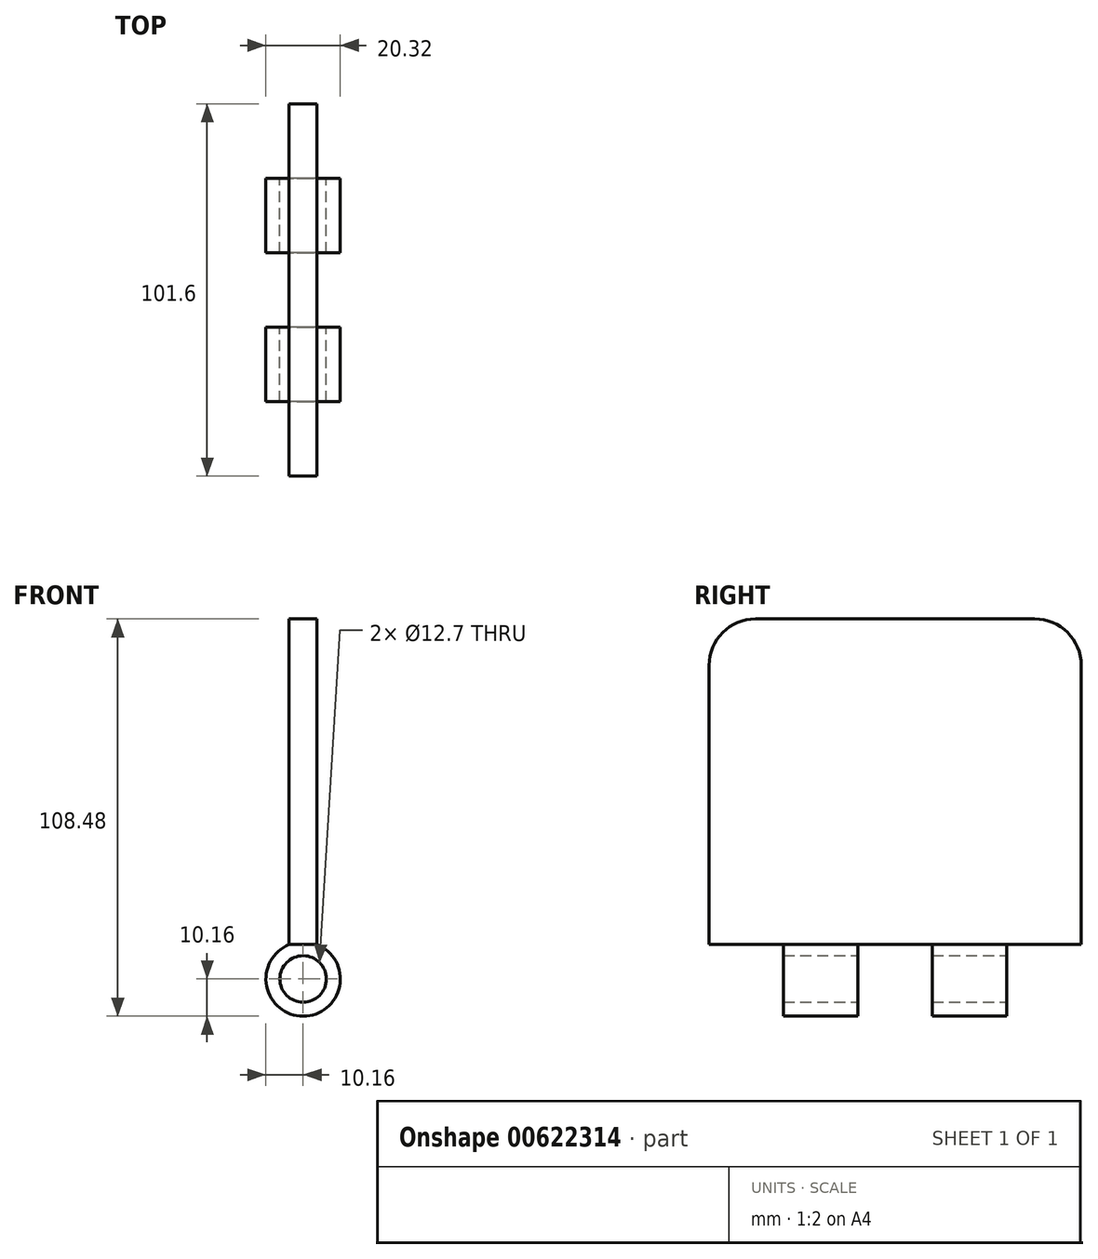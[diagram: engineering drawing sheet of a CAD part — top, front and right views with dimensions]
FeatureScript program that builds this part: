
annotation { "Feature Type Name" : "Feature", "Feature Type Description" : "" }
export const myFeature = defineFeature(function(context is Context, id is Id, definition is map)
    precondition{}
    {
        {
            var Q0;
            Q0=qCreatedBy(makeId("Front.planeOp"),FACE);
            var sketch = newSketch(context, id + "F0", { "sketchPlane" : qUnion([Q0])});
            skLineSegment(sketch, "E0", {"start": v(-3.81, 9.42) * mm, "end": v(-3.81, 98.32) * mm});
            skLineSegment(sketch, "E1", {"start": v(-3.81, 98.32) * mm, "end": v(3.8, 98.32) * mm});
            skLineSegment(sketch, "E2", {"start": v(3.8, 98.32) * mm, "end": v(3.81, 9.42) * mm});
            skArc(sketch, "E3", {"start": v(-3.81, 9.42) * mm, "mid": v(0, -10.16) * mm, "end": v(3.81, 9.42) * mm});
            skSolve(sketch);
        }
        {
            var Q0;
            Q0=makeQuery(id+"F0.imprint","IMPRINT",FACE,{"disambiguationData":[TD([[makeQuery(id+"F0.imprint","IMPRINT",EDGE,{"derivedFrom":sQuery(id+"F0.wireOp",EDGE,"E0")}),-1.0]])]});
            extrude(context, id + "F1", {"entities" : qUnion([Q0]), "depth" : 101.6 * mm, "offsetDistance" : 25.4 * mm, "symmetric" : true});
        }
        {
            var Q0;
            Q0=makeQuery(id+"F1.opExtrude","CAP_EDGE",EDGE,{"disambiguationData":[OSD([sQuery(id+"F0.wireOp",EDGE,"E1")])],"isStart":false});
            var Q1;
            Q1=makeQuery(id+"F1.opExtrude","CAP_EDGE",EDGE,{"disambiguationData":[OSD([sQuery(id+"F0.wireOp",EDGE,"E1")])],"isStart":true});
            fillet(context, id + "F2", {"entities" : qUnion([Q0, Q1]), "radius" : 12.7 * mm, "tangentPropagation" : true, "allowEdgeOverflow" : false});
        }
        {
            var Q0;
            Q0=makeQuery(id+"F1.opExtrude","CAP_FACE",FACE,{"disambiguationData":[OSD([sQuery(id+"F0.wireOp",EDGE,"E0"),sQuery(id+"F0.wireOp",EDGE,"E1"),sQuery(id+"F0.wireOp",EDGE,"E2"),sQuery(id+"F0.wireOp",EDGE,"E3")])],"isStart":true});
            var sketch = newSketch(context, id + "F3", { "sketchPlane" : qUnion([Q0])});
            skCircle(sketch, "E4", {"center": v(0, 0) * mm, "radius": 6.35 * mm});
            skSolve(sketch);
        }
        {
            var Q0;
            Q0=makeQuery(id+"F3.imprint","IMPRINT",FACE,{"disambiguationData":[TD([[makeQuery(id+"F3.imprint","IMPRINT",EDGE,{"derivedFrom":sQuery(id+"F3.wireOp",EDGE,"E4")}),1.0]])]});
            extrude(context, id + "F4", {"entities" : qUnion([Q0]), "operationType" : NewBodyOperationType.REMOVE, "endBound" : BoundingType.THROUGH_ALL, "oppositeDirection" : true, "depth" : 25.4 * mm, "offsetDistance" : 25.4 * mm});
        }
        {
            var Q0;
            Q0=makeQuery(id+"F1.opExtrude","SWEPT_FACE",FACE,{"disambiguationData":[OSD([sQuery(id+"F0.wireOp",EDGE,"E0")])]});
            var sketch = newSketch(context, id + "F5", { "sketchPlane" : qUnion([Q0])});
            skLineSegment(sketch, "E5", {"start": v(-50.8, 9.42) * mm, "end": v(-50.8, -28.68) * mm});
            skLineSegment(sketch, "E6", {"start": v(-50.8, -22.1) * mm, "end": v(-30.48, -22.1) * mm});
            skLineSegment(sketch, "E7", {"start": v(50.8, 9.42) * mm, "end": v(50.8, -28.68) * mm});
            skLineSegment(sketch, "E8", {"start": v(50.8, -28.68) * mm, "end": v(30.48, -28.68) * mm});
            skLineSegment(sketch, "E9", {"start": v(-10.16, -20.94) * mm, "end": v(-10.16, 15.13) * mm});
            skLineSegment(sketch, "E10", {"start": v(-10.16, 15.13) * mm, "end": v(10.16, 15.13) * mm});
            skLineSegment(sketch, "E11", {"start": v(10.16, 15.13) * mm, "end": v(10.16, -22.94) * mm});
            skLineSegment(sketch, "E12", {"start": v(10.16, -22.94) * mm, "end": v(-10.16, -22.94) * mm});
            skLineSegment(sketch, "E13", {"start": v(-10.16, -22.94) * mm, "end": v(-10.16, -20.94) * mm});
            skLineSegment(sketch, "E14", {"start": v(-30.48, 15.65) * mm, "end": v(-50.8, 15.65) * mm});
            skLineSegment(sketch, "E15", {"start": v(-50.8, 15.65) * mm, "end": v(-50.8, -9.63) * mm});
            skLineSegment(sketch, "E16", {"start": v(30.48, 15.3) * mm, "end": v(50.8, 15.3) * mm});
            skLineSegment(sketch, "E17", {"start": v(50.8, 15.3) * mm, "end": v(50.8, -28.68) * mm});
            skLineSegment(sketch, "E18", {"start": v(30.48, 15.3) * mm, "end": v(30.48, -28.68) * mm});
            skLineSegment(sketch, "E19", {"start": v(-30.48, -22.1) * mm, "end": v(-30.48, 15.65) * mm});
            skSolve(sketch);
        }
        {
            var Q0;
            {var subQ0=sQuery(id+"F5.wireOp",EDGE,"E8");Q0=makeQuery(id+"F5.imprint","IMPRINT",FACE,{"disambiguationData":[TD([[makeQuery(id+"F5.imprint","IMPRINT",EDGE,{"derivedFrom":subQ0}),-1.0]])]});}
            var Q1;
            {var subQ1=sQuery(id+"F5.wireOp",EDGE,"E12");Q1=makeQuery(id+"F5.imprint","IMPRINT",FACE,{"disambiguationData":[TD([[makeQuery(id+"F5.imprint","IMPRINT",EDGE,{"derivedFrom":subQ1}),-1.0]])]});}
            var Q2;
            {var subQ1=sQuery(id+"F5.wireOp",EDGE,"E6");Q2=makeQuery(id+"F5.imprint","IMPRINT",FACE,{"disambiguationData":[TD([[makeQuery(id+"F5.imprint","IMPRINT",EDGE,{"derivedFrom":subQ1}),1.0]])]});}
            extrude(context, id + "F6", {"entities" : qUnion([Q0, Q1, Q2]), "operationType" : NewBodyOperationType.REMOVE, "oppositeDirection" : true, "depth" : 177.8 * mm, "offsetDistance" : 25.4 * mm, "symmetric" : true});
        }
    });
